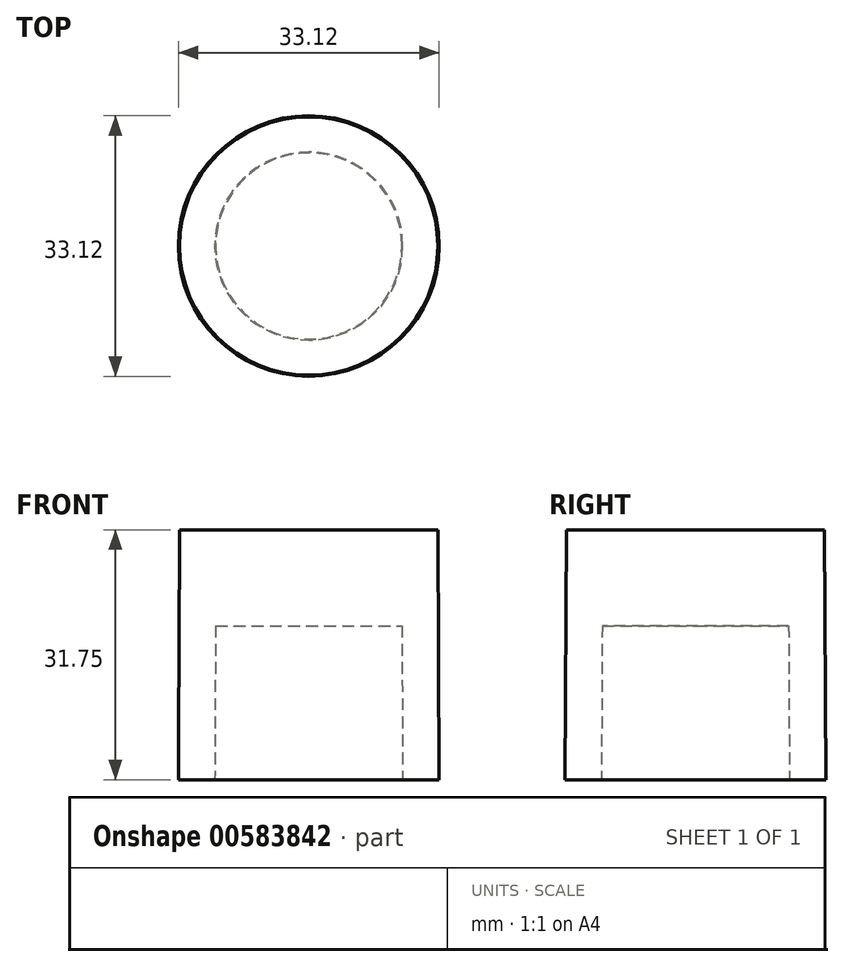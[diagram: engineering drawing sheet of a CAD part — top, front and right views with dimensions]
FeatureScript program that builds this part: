
annotation { "Feature Type Name" : "Feature", "Feature Type Description" : "" }
export const myFeature = defineFeature(function(context is Context, id is Id, definition is map)
    precondition{}
    {
        {
            var Q0;
            Q0=qCreatedBy(makeId("Front.planeOp"),FACE);
            var sketch = newSketch(context, id + "F0", { "sketchPlane" : qUnion([Q0])});
            skLineSegment(sketch, "E0", {"start": v(0, 0) * mm, "end": v(-16.56, 0) * mm});
            skLineSegment(sketch, "E1", {"start": v(0, 0) * mm, "end": v(0, 31.75) * mm});
            skLineSegment(sketch, "E2", {"start": v(0, 31.75) * mm, "end": v(-16.4, 31.75) * mm});
            skLineSegment(sketch, "E3", {"start": v(-16.4, 31.75) * mm, "end": v(-16.56, 0) * mm});
            skSolve(sketch);
        }
        {
            var Q0;
            Q0 = qSketchRegion(id + "F0", true);
            var Q1;
            Q1 = qConstructionFilter(qBodyType(qCreatedBy(id + "F0" ,EDGE), BodyType.WIRE), ConstructionObject.NO);
            var Q2;
            Q2=sQuery(id+"F0.wireOp",EDGE,"E1");
            revolve(context, id + "F1", {"entities" : qUnion([Q0]), "surfaceEntities" : qUnion([Q1]), "axis" : qUnion([Q2]), "revolveType" : RevolveType.FULL});
        }
        {
            var Q0;
            Q0=qCreatedBy(makeId("Front.planeOp"),FACE);
            var sketch = newSketch(context, id + "F2", { "sketchPlane" : qUnion([Q0])});
            skLineSegment(sketch, "E4", {"start": v(0, 0) * mm, "end": v(-11.94, 0) * mm});
            skLineSegment(sketch, "E5", {"start": v(0, 0) * mm, "end": v(0, 19.56) * mm});
            skLineSegment(sketch, "E6", {"start": v(0, 19.56) * mm, "end": v(-11.84, 19.56) * mm});
            skLineSegment(sketch, "E7", {"start": v(-11.84, 19.56) * mm, "end": v(-11.94, 0) * mm});
            skSolve(sketch);
        }
        {
            var Q0;
            Q0 = qSketchRegion(id + "F2", true);
            var Q1;
            Q1=sQuery(id+"F2.wireOp",EDGE,"E5");
            revolve(context, id + "F3", {"operationType" : NewBodyOperationType.REMOVE, "entities" : qUnion([Q0]), "axis" : qUnion([Q1]), "revolveType" : RevolveType.FULL});
        }
    });
